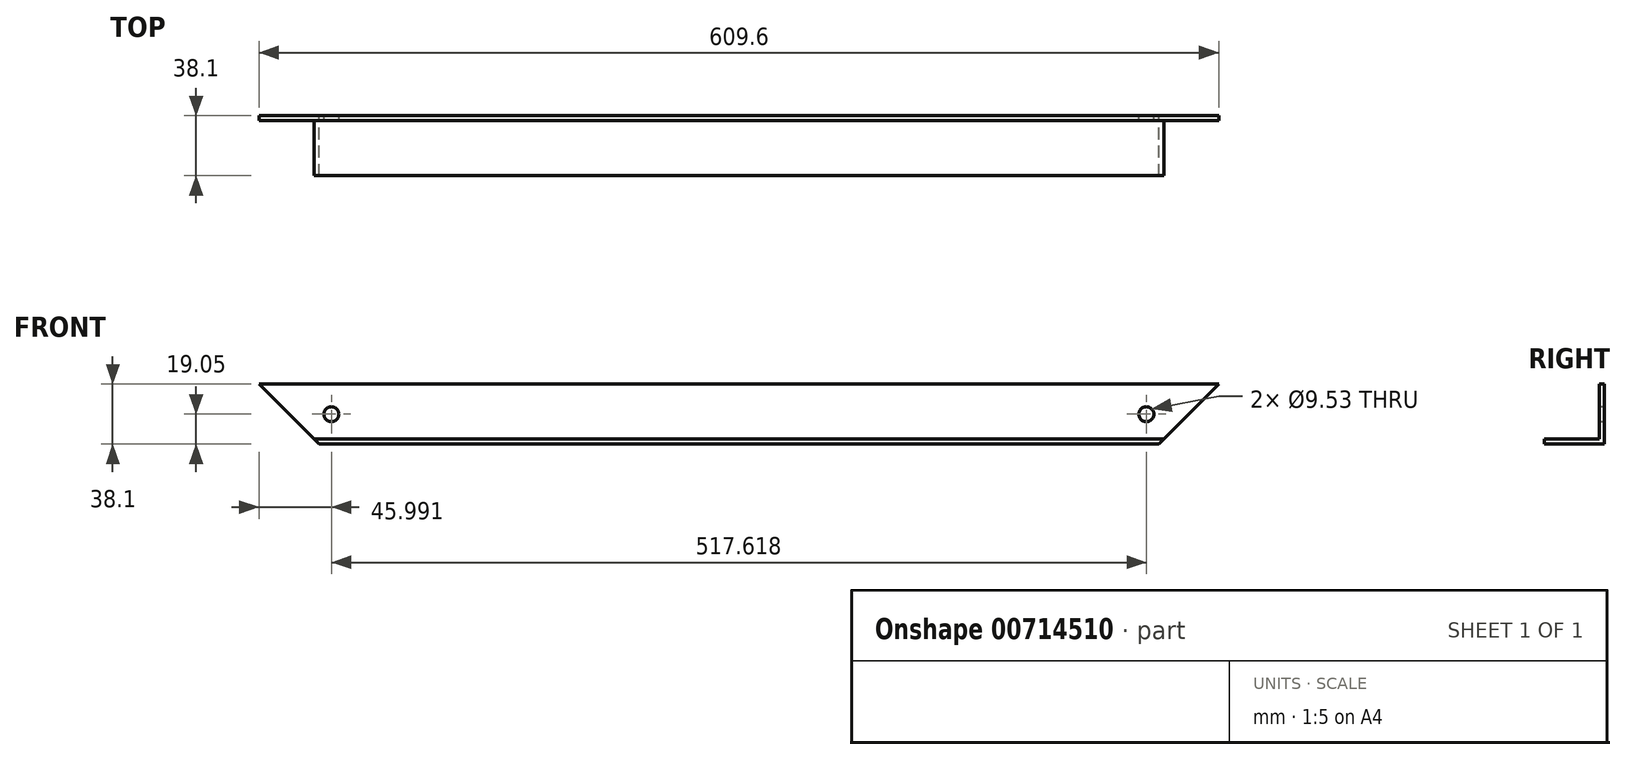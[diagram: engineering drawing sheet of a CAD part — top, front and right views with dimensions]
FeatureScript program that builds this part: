
annotation { "Feature Type Name" : "Feature", "Feature Type Description" : "" }
export const myFeature = defineFeature(function(context is Context, id is Id, definition is map)
    precondition{}
    {
        {
            var Q0;
            Q0=qCreatedBy(makeId("Right.planeOp"),FACE);
            var sketch = newSketch(context, id + "F0", { "sketchPlane" : qUnion([Q0])});
            skLineSegment(sketch, "E0", {"start": v(0, 0) * mm, "end": v(38.1, 0) * mm});
            skLineSegment(sketch, "E1", {"start": v(38.1, 0) * mm, "end": v(38.1, 38.1) * mm});
            skLineSegment(sketch, "E2", {"start": v(38.1, 38.1) * mm, "end": v(34.92, 38.1) * mm});
            skLineSegment(sketch, "E3", {"start": v(34.92, 38.1) * mm, "end": v(34.92, 3.18) * mm});
            skLineSegment(sketch, "E4", {"start": v(34.92, 3.18) * mm, "end": v(0, 3.18) * mm});
            skLineSegment(sketch, "E5", {"start": v(0, 3.18) * mm, "end": v(0, 0) * mm});
            skSolve(sketch);
        }
        {
            var Q0;
            Q0=makeQuery(id+"F0.imprint","IMPRINT",FACE,{"disambiguationData":[TD([[makeQuery(id+"F0.imprint","IMPRINT",EDGE,{"derivedFrom":sQuery(id+"F0.wireOp",EDGE,"E0")}),1.0]])]});
            extrude(context, id + "F1", {"entities" : qUnion([Q0]), "depth" : 609.6 * mm, "offsetDistance" : 25.4 * mm});
        }
        {
            var Q0;
            Q0=makeQuery(id+"F1.opExtrude","SWEPT_FACE",FACE,{"disambiguationData":[OSD([sQuery(id+"F0.wireOp",EDGE,"E1")])]});
            var sketch = newSketch(context, id + "F2", { "sketchPlane" : qUnion([Q0])});
            skLineSegment(sketch, "E6", {"start": v(-609.6, 38.1) * mm, "end": v(-571.5, 0) * mm});
            skLineSegment(sketch, "E7", {"start": v(-571.5, 0) * mm, "end": v(-609.6, 0) * mm});
            skLineSegment(sketch, "E8", {"start": v(-609.6, 0) * mm, "end": v(-609.6, 38.1) * mm});
            skLineSegment(sketch, "E9", {"start": v(0, 38.1) * mm, "end": v(-38.1, 0) * mm});
            skLineSegment(sketch, "E10", {"start": v(-38.1, 0) * mm, "end": v(0, 0) * mm});
            skLineSegment(sketch, "E11", {"start": v(0, 0) * mm, "end": v(0, 38.1) * mm});
            skSolve(sketch);
        }
        {
            var Q0;
            Q0=makeQuery(id+"F2.imprint","IMPRINT",FACE,{"disambiguationData":[TD([[makeQuery(id+"F2.imprint","IMPRINT",EDGE,{"derivedFrom":sQuery(id+"F2.wireOp",EDGE,"E6")}),-1.0]])]});
            var Q1;
            Q1=makeQuery(id+"F2.imprint","IMPRINT",FACE,{"disambiguationData":[TD([[makeQuery(id+"F2.imprint","IMPRINT",EDGE,{"derivedFrom":sQuery(id+"F2.wireOp",EDGE,"E9")}),1.0]])]});
            extrude(context, id + "F3", {"entities" : qUnion([Q0, Q1]), "operationType" : NewBodyOperationType.REMOVE, "endBound" : BoundingType.THROUGH_ALL, "oppositeDirection" : true, "depth" : 25.4 * mm, "offsetDistance" : 25.4 * mm});
        }
        {
            var Q0;
            Q0=makeQuery(id+"F1.opExtrude","SWEPT_FACE",FACE,{"disambiguationData":[OSD([sQuery(id+"F0.wireOp",EDGE,"E1")])]});
            var sketch = newSketch(context, id + "F4", { "sketchPlane" : qUnion([Q0])});
            skCircle(sketch, "E12", {"center": v(-563.6, 19.05) * mm, "radius": 4.76 * mm});
            skCircle(sketch, "E13", {"center": v(-46, 19.05) * mm, "radius": 4.76 * mm});
            skSolve(sketch);
        }
        {
            var Q0;
            Q0=makeQuery(id+"F4.imprint","IMPRINT",FACE,{"disambiguationData":[TD([[makeQuery(id+"F4.imprint","IMPRINT",EDGE,{"derivedFrom":sQuery(id+"F4.wireOp",EDGE,"E13")}),1.0]])]});
            var Q1;
            Q1=makeQuery(id+"F4.imprint","IMPRINT",FACE,{"disambiguationData":[TD([[makeQuery(id+"F4.imprint","IMPRINT",EDGE,{"derivedFrom":sQuery(id+"F4.wireOp",EDGE,"E12")}),1.0]])]});
            extrude(context, id + "F5", {"entities" : qUnion([Q0, Q1]), "operationType" : NewBodyOperationType.REMOVE, "endBound" : BoundingType.THROUGH_ALL, "oppositeDirection" : true, "depth" : 25.4 * mm, "offsetDistance" : 25.4 * mm});
        }
    });
